# Revit family: 306_978155e8eab34d70b5c99dea683e7f
name_source: partatom
category: Pipe Accessories
units: mm (PartAtom-declared; Revit-internal decimal feet)

## family parameters
Always vertical = Yes
Cut with Voids When Loaded = No
Part Type = Valve - Breaks Into
Round Connector Dimension = Use Diameter
Shared = No
Work Plane-Based = No

## types (4) — shared parameters
B = 62 mm  [stored 0.203412 ft]
C = 60 mm  [stored 0.19685 ft]
CAT0 = Yes
CT2 = 24 mm  [stored 0.0787402 ft]
Description = Thermostatic mixing valve VTA532, PN10 external thread
L2D = 70 mm
L2D_Min = 3048 mm  [stored 10 ft]
LT2 = 35 mm  [stored 0.114829 ft]
MC = No
Manufacturer = ESBE
QmdConnectorList = 301;D;302;D
URL = http://www.esbe.eu
W1 = 21 mm  [stored 0.0688976 ft]
WT2 = 28 mm  [stored 0.0918635 ft]
X1 = 2 mm  [stored 0.00656168 ft]
X2 = 7 mm  [stored 0.0229659 ft]
X3 = 66 mm  [stored 0.216535 ft]
X4 = 62 mm  [stored 0.203412 ft]
magiPartTypeId = 306
magiProductFamilyId = 978155e8eab34d70b5c99dea683e7f

## per-type parameters (varying)
| type | A | A__ve | D | DT2 | R2 | W2D | Z1 | Z1__ve | Z2 | magiProductId |
| VTA532 35-50°C G1 1/4-2,5 | 38 mm | -38 mm | 32 mm | 16 mm  [stored 0.0524934 ft] | 14 mm  [stored 0.0459318 ft] | 32 mm  [stored 0.104987 ft] | 25 mm  [stored 0.082021 ft] | -25 mm  [stored -0.082021 ft] | 8 mm  [stored 0.0262467 ft] | 2209afe56efd4cc7b357f7006d8876 |
| VTA532 45-65°C G1-2,3 | 35 mm  [stored 0.114829 ft] | -35 mm  [stored -0.114829 ft] | 25 mm | 13 mm  [stored 0.0426509 ft] | 11 mm  [stored 0.0360892 ft] | 25 mm  [stored 0.082021 ft] | 27 mm | -27 mm | 9 mm  [stored 0.0295276 ft] | 676d40a7be4440f3b8b9e238eb4278 |
| VTA532 45-65°C G1 1/4-2,5 | 38 mm | -38 mm | 32 mm | 16 mm  [stored 0.0524934 ft] | 14 mm  [stored 0.0459318 ft] | 32 mm  [stored 0.104987 ft] | 25 mm  [stored 0.082021 ft] | -25 mm  [stored -0.082021 ft] | 8 mm  [stored 0.0262467 ft] | be34adaeb16f41369067549822c01c |
| VTA532 35-50°C G1-2,3 | 35 mm  [stored 0.114829 ft] | -35 mm  [stored -0.114829 ft] | 25 mm | 13 mm  [stored 0.0426509 ft] | 11 mm  [stored 0.0360892 ft] | 25 mm  [stored 0.082021 ft] | 27 mm | -27 mm | 9 mm  [stored 0.0295276 ft] | 0fbc0dcc90fd480f9f9617034d860e |

note: column(s) folded — value = type name in every type: magiProductCode

note: [stored X ft] marks values corroborated as IEEE doubles in the binary element streams (Revit-internal decimal feet)

## geometry (parser evidence)
native form markers: Sweep x1
no freeform markers — native parametric forms only
